# Revit family: QPTW
name_source: partatom
category: Mechanical Equipment
revit_build: Autodesk Revit 2018 (Build: 20170223_1515(x64)
units: mm (PartAtom-declared; Revit-internal decimal feet)

## family parameters
Always vertical = Yes
Cut with Voids When Loaded = No
Part Type = Normal
Room Calculation Point = No
Round Connector Dimension = Use Radius
Shared = No
Work Plane-Based = No

## types (104) — shared parameters
Description = Series Fan Powered Air Terminal with Hot Water Coil
Enclosure Depth = 6 1/2"
Filter = 1"
HWC B = 1 3/4"
HWC C = 1 5/8"
HWC Length = 4"
HWC V = 9/16"
Manufacturer = Anemostat
Model = QPTW
URL = http://www.anemostat.com

## per-type parameters (varying)
| type | Diameter | Duct Inlet Radius | HWC "X" | HWC "Y" | HWC Conn Dia | HWC R | HWC-Z | Height | Induction | Induction Height "D" | Induction Width "C" | Length | Q5 Sound Elbow | Q5B | Q5Q | Radius | Width |
| 25012 QPTW 1/2-hp - 12" 1RC with S/Elbow | 11 7/8" | 6" | 20" | 17 1/2" | 7/8" | 7/16" | 12 1/4" | 18" | No | 16" | 17" | 34" | Yes | 20" | 18" | 5 15/16" | 40" |
| 37512 QPTW 3/4-hp - 12" 1RC W/Out S/Elbow | 11 7/8" | 6" | 24" | 17 1/2" | 7/8" | 7/16" | 12 1/4" | 20" | Yes | 18" | 21" | 40" | No | 23" | 20" | 5 15/16" | 46" |
| 37512 QPTW 3/4-hp - 12" 2RC W/Out S/Elbow | 11 7/8" | 6" | 24" | 17 1/2" | 7/8" | 7/16" | 13 1/2" | 20" | Yes | 18" | 21" | 40" | No | 23" | 20" | 5 15/16" | 46" |
| 37512 QPTW 3/4-hp - 12" 1RC with S/Elbow | 11 7/8" | 6" | 24" | 17 1/2" | 7/8" | 7/16" | 12 1/4" | 20" | No | 18" | 21" | 40" | Yes | 23" | 20" | 5 15/16" | 46" |
| 37512 QPTW 3/4-hp - 12" 2RC with S/Elbow | 11 7/8" | 6" | 24" | 17 1/2" | 7/8" | 7/16" | 13 1/2" | 20" | No | 18" | 21" | 40" | Yes | 23" | 20" | 5 15/16" | 46" |
| 37514 QPTW 3/4-hp - 14" 1RC W/Out S/Elbow | 13 7/8" | 7" | 24" | 17 1/2" | 7/8" | 7/16" | 12 1/4" | 20" | Yes | 18" | 21" | 40" | No | 23" | 20" | 6 15/16" | 46" |
| 37514 QPTW 3/4-hp - 14" 1RC with S/Elbow | 13 7/8" | 7" | 24" | 17 1/2" | 7/8" | 7/16" | 12 1/4" | 20" | No | 18" | 21" | 40" | Yes | 23" | 20" | 6 15/16" | 46" |
| 37514 QPTW 3/4-hp - 14" 2RC W/Out S/Elbow | 13 7/8" | 7" | 24" | 17 1/2" | 7/8" | 7/16" | 13 1/2" | 20" | Yes | 18" | 21" | 40" | No | 23" | 20" | 6 15/16" | 46" |
| 37514 QPTW 3/4-hp - 14" 2RC with S/Elbow | 13 7/8" | 7" | 24" | 17 1/2" | 7/8" | 7/16" | 13 1/2" | 20" | No | 18" | 21" | 40" | Yes | 23" | 20" | 6 15/16" | 46" |
| 37516 QPTW 3/4-hp - 16" 1RC W/Out S/Elbow | 15 7/8" | 8" | 24" | 17 1/2" | 7/8" | 7/16" | 12 1/4" | 20" | Yes | 18" | 21" | 40" | No | 23" | 20" | 7 15/16" | 46" |
| 37516 QPTW 3/4-hp - 16" 1RC with S/Elbow | 15 7/8" | 8" | 24" | 17 1/2" | 7/8" | 7/16" | 12 1/4" | 20" | No | 18" | 21" | 40" | Yes | 23" | 20" | 7 15/16" | 46" |
| 37516 QPTW 3/4-hp - 16" 2RC W/Out S/Elbow | 15 7/8" | 8" | 24" | 17 1/2" | 7/8" | 7/16" | 13 1/2" | 20" | Yes | 18" | 21" | 40" | No | 23" | 20" | 7 15/16" | 46" |
| 37516 QPTW 3/4-hp - 16" 2RC with S/Elbow | 15 7/8" | 8" | 24" | 17 1/2" | 7/8" | 7/16" | 13 1/2" | 20" | No | 18" | 21" | 40" | Yes | 23" | 20" | 7 15/16" | 46" |
| 12509 QPTW 1/4-hp - 09" 1RC with S/Elbow | 8 7/8" | 4" | 16" | 15" | 1/2" | 1/4" | 12 1/4" | 15" | No | 12" | 13" | 30" | Yes | 18" | 18" | 4 7/16" | 34" |
| 12509 QPTW 1/4-hp - 09" 1RC W/Out S/Elbow | 8 7/8" | 4" | 16" | 15" | 1/2" | 1/4" | 12 1/4" | 15" | Yes | 12" | 13" | 30" | No | 18" | 18" | 4 7/16" | 34" |
| 25012 QPTW 1/2-hp - 12" 1RC W/Out S/Elbow | 11 7/8" | 6" | 20" | 17 1/2" | 7/8" | 7/16" | 12 1/4" | 18" | Yes | 16" | 17" | 34" | No | 20" | 18" | 5 15/16" | 40" |
| 35016 QPTW 1/2-hp - 16" 1RC with S/Elbow | 15 7/8" | 8" | 24" | 17 1/2" | 7/8" | 7/16" | 12 1/4" | 20" | No | 18" | 21" | 40" | Yes | 23" | 20" | 7 15/16" | 46" |
| 35016 QPTW 1/2-hp - 16" 2RC W/Out S/Elbow | 15 7/8" | 8" | 24" | 17 1/2" | 7/8" | 7/16" | 13 1/2" | 20" | Yes | 18" | 21" | 40" | No | 23" | 20" | 7 15/16" | 46" |
| 35016 QPTW 1/2-hp - 16" 1RC W/Out S/Elbow | 15 7/8" | 8" | 24" | 17 1/2" | 7/8" | 7/16" | 12 1/4" | 20" | Yes | 18" | 21" | 40" | No | 23" | 20" | 7 15/16" | 46" |
| 35016 QPTW 1/2-hp - 16" 2RC with S/Elbow | 15 7/8" | 8" | 24" | 17 1/2" | 7/8" | 7/16" | 13 1/2" | 20" | No | 18" | 21" | 40" | Yes | 23" | 20" | 7 15/16" | 46" |
| 35014 QPTW 1/2-hp - 14" 1RC W/Out S/Elbow | 13 7/8" | 7" | 24" | 17 1/2" | 7/8" | 7/16" | 12 1/4" | 20" | Yes | 18" | 21" | 40" | No | 23" | 20" | 6 15/16" | 46" |
| 35014 QPTW 1/2-hp - 14" 1RC with S/Elbow | 13 7/8" | 7" | 24" | 17 1/2" | 7/8" | 7/16" | 12 1/4" | 20" | No | 18" | 21" | 40" | Yes | 23" | 20" | 6 15/16" | 46" |
| 35014 QPTW 1/2-hp - 14" 2RC W/Out S/Elbow | 15 7/8" | 8" | 24" | 17 1/2" | 7/8" | 7/16" | 13 1/2" | 20" | Yes | 18" | 21" | 40" | No | 23" | 20" | 7 15/16" | 46" |
| 35014 QPTW 1/2-hp - 14" 2RC with S/Elbow | 15 7/8" | 8" | 24" | 17 1/2" | 7/8" | 7/16" | 13 1/2" | 20" | No | 18" | 21" | 40" | Yes | 23" | 20" | 7 15/16" | 46" |
| 35012 QPTW 1/2-hp - 12" 2RC with S/Elbow | 11 7/8" | 6" | 24" | 17 1/2" | 7/8" | 7/16" | 13 1/2" | 20" | No | 18" | 21" | 40" | Yes | 23" | 20" | 5 15/16" | 46" |
| 35012 QPTW 1/2-hp - 12" 2RC W/Out S/Elbow | 11 7/8" | 6" | 24" | 17 1/2" | 7/8" | 7/16" | 13 1/2" | 20" | Yes | 18" | 21" | 40" | No | 23" | 20" | 5 15/16" | 46" |
| 35012 QPTW 1/2-hp - 12" 1RC with S/Elbow | 11 7/8" | 6" | 24" | 17 1/2" | 7/8" | 7/16" | 12 1/4" | 20" | No | 18" | 21" | 40" | Yes | 23" | 20" | 5 15/16" | 46" |
| 35012 QPTW 1/2-hp - 12" 1RC W/Out S/Elbow | 11 7/8" | 6" | 24" | 17 1/2" | 7/8" | 7/16" | 12 1/4" | 20" | Yes | 18" | 21" | 40" | No | 23" | 20" | 5 15/16" | 46" |
| 31016 QPTW 1-hp - 16" 2RC with S/Elbow | 15 7/8" | 8" | 24" | 17 1/2" | 7/8" | 7/16" | 13 1/2" | 20" | No | 18" | 21" | 40" | Yes | 23" | 20" | 7 15/16" | 46" |
| 31016 QPTW 1-hp - 16" 2RC W/Out S/Elbow | 15 7/8" | 8" | 24" | 17 1/2" | 7/8" | 7/16" | 13 1/2" | 20" | Yes | 18" | 21" | 40" | No | 23" | 20" | 7 15/16" | 46" |
| 31016 QPTW 1-hp - 16" 1RC with S/Elbow | 15 7/8" | 8" | 24" | 17 1/2" | 7/8" | 7/16" | 12 1/4" | 20" | No | 18" | 21" | 40" | Yes | 23" | 20" | 7 15/16" | 46" |
| 31016 QPTW 1-hp - 16" 1RC W/Out S/Elbow | 15 7/8" | 8" | 24" | 17 1/2" | 7/8" | 7/16" | 12 1/4" | 20" | Yes | 18" | 21" | 40" | No | 23" | 20" | 7 15/16" | 46" |
| 31014 QPTW 1-hp - 14" 1RC W/Out S/Elbow | 13 7/8" | 7" | 24" | 17 1/2" | 7/8" | 7/16" | 12 1/4" | 20" | Yes | 18" | 21" | 40" | No | 23" | 20" | 6 15/16" | 46" |
| 31014 QPTW 1-hp - 14" 1RC with S/Elbow | 13 7/8" | 7" | 24" | 17 1/2" | 7/8" | 7/16" | 12 1/4" | 20" | No | 18" | 21" | 40" | Yes | 23" | 20" | 6 15/16" | 46" |
| 31014 QPTW 1-hp - 14" 2RC W/Out S/Elbow | 13 7/8" | 7" | 24" | 17 1/2" | 7/8" | 7/16" | 13 1/2" | 20" | Yes | 18" | 21" | 40" | No | 23" | 20" | 6 15/16" | 46" |
| 31014 QPTW 1-hp - 14" 2RC with S/Elbow | 13 7/8" | 7" | 24" | 17 1/2" | 7/8" | 7/16" | 13 1/2" | 20" | No | 18" | 21" | 40" | Yes | 23" | 20" | 6 15/16" | 46" |
| 31012 QPTW 1-hp - 12" 1RC W/Out S/Elbow | 11 7/8" | 6" | 24" | 17 1/2" | 7/8" | 7/16" | 12 1/4" | 20" | Yes | 18" | 21" | 40" | No | 23" | 20" | 5 15/16" | 46" |
| 31012 QPTW 1-hp - 12" 1RC with S/Elbow | 11 7/8" | 6" | 24" | 17 1/2" | 7/8" | 7/16" | 12 1/4" | 20" | No | 18" | 21" | 40" | Yes | 23" | 20" | 5 15/16" | 46" |
| 31012 QPTW 1-hp - 12" 2RC W/Out S/Elbow | 11 7/8" | 6" | 24" | 17 1/2" | 7/8" | 7/16" | 13 1/2" | 20" | Yes | 18" | 21" | 40" | No | 23" | 20" | 5 15/16" | 46" |
| 31012 QPTW 1-hp - 12" 2RC with S/Elbow | 11 7/8" | 6" | 24" | 17 1/2" | 7/8" | 7/16" | 13 1/2" | 20" | No | 18" | 21" | 40" | Yes | 23" | 20" | 5 15/16" | 46" |
| 25012 QPTW 1/2-hp - 12" 2RC W/Out S/Elbow | 11 7/8" | 6" | 20" | 17 1/2" | 7/8" | 7/16" | 13 1/2" | 18" | Yes | 16" | 17" | 34" | No | 20" | 18" | 5 15/16" | 40" |
| 25012 QPTW 1/2-hp - 12" 2RC with S/Elbow | 11 7/8" | 6" | 20" | 17 1/2" | 7/8" | 7/16" | 13 1/2" | 18" | No | 16" | 17" | 34" | Yes | 20" | 18" | 5 15/16" | 40" |
| 25010 QPTW 1/2-hp - 10" 2RC with S/Elbow | 9 7/8" | 5" | 20" | 17 1/2" | 7/8" | 7/16" | 13 1/2" | 18" | No | 16" | 17" | 34" | Yes | 20" | 18" | 4 15/16" | 40" |
| 25010 QPTW 1/2-hp - 10" 2RC W/Out S/Elbow | 9 7/8" | 5" | 20" | 17 1/2" | 7/8" | 7/16" | 13 1/2" | 18" | Yes | 16" | 17" | 34" | No | 20" | 18" | 4 15/16" | 40" |
| 25010 QPTW 1/2-hp - 10" 1RC with S/Elbow | 9 7/8" | 5" | 20" | 17 1/2" | 7/8" | 7/16" | 12 1/4" | 18" | No | 16" | 17" | 34" | Yes | 20" | 18" | 4 15/16" | 40" |
| 25010 QPTW 1/2-hp - 10" 1RC W/Out S/Elbow | 9 7/8" | 5" | 20" | 17 1/2" | 7/8" | 7/16" | 12 1/4" | 18" | Yes | 16" | 17" | 34" | No | 20" | 18" | 4 15/16" | 40" |
| 25009 QPTW 1/2-hp - 09" 1RC W/Out S/Elbow | 8 7/8" | 4" | 20" | 17 1/2" | 7/8" | 7/16" | 12 1/4" | 18" | Yes | 16" | 17" | 34" | No | 20" | 18" | 4 7/16" | 40" |
| 25009 QPTW 1/2-hp - 09" 1RC with S/Elbow | 8 7/8" | 4" | 20" | 17 1/2" | 7/8" | 7/16" | 12 1/4" | 18" | No | 16" | 17" | 34" | Yes | 20" | 18" | 4 7/16" | 40" |
| 25009 QPTW 1/2-hp - 09" 2RC W/Out S/Elbow | 8 7/8" | 4" | 20" | 17 1/2" | 7/8" | 7/16" | 13 1/2" | 18" | Yes | 16" | 17" | 34" | No | 20" | 18" | 4 7/16" | 40" |
| 25009 QPTW 1/2-hp - 09" 2RC with S/Elbow | 8 7/8" | 4" | 20" | 17 1/2" | 7/8" | 7/16" | 13 1/2" | 18" | No | 16" | 17" | 34" | Yes | 20" | 18" | 4 7/16" | 40" |
| 12509 QPTW 1/4-hp - 09" 2RC W/Out S/Elbow | 8 7/8" | 4" | 16" | 15" | 1/2" | 1/4" | 13 1/2" | 15" | Yes | 12" | 13" | 30" | No | 18" | 18" | 4 7/16" | 34" |
| 12509 QPTW 1/4-hp - 09" 2RC with S/Elbow | 8 7/8" | 4" | 16" | 15" | 1/2" | 1/4" | 13 1/2" | 15" | No | 12" | 13" | 30" | Yes | 18" | 18" | 4 7/16" | 34" |
| 22512 QPTW 1/4-hp - 12" 1RC W/Out S/Elbow | 11 7/8" | 6" | 20" | 17 1/2" | 7/8" | 7/16" | 12 1/4" | 18" | Yes | 16" | 17" | 34" | No | 20" | 18" | 5 15/16" | 40" |
| 22512 QPTW 1/4-hp - 12" 1RC with S/Elbow | 11 7/8" | 6" | 20" | 17 1/2" | 7/8" | 7/16" | 12 1/4" | 18" | No | 16" | 17" | 34" | Yes | 20" | 18" | 5 15/16" | 40" |
| 22512 QPTW 1/4-hp - 12" 2RC W/Out S/Elbow | 11 7/8" | 6" | 20" | 17 1/2" | 7/8" | 7/16" | 13 1/2" | 18" | No | 16" | 17" | 34" | Yes | 20" | 18" | 5 15/16" | 40" |
| 22512 QPTW 1/4-hp - 12" 2RC with S/Elbow | 11 7/8" | 6" | 20" | 17 1/2" | 7/8" | 7/16" | 13 1/2" | 18" | No | 16" | 17" | 34" | Yes | 20" | 18" | 5 15/16" | 40" |
| 22510 QPTW 1/4-hp - 10" 1RC W/Out S/Elbow | 9 7/8" | 5" | 20" | 17 1/2" | 7/8" | 7/16" | 12 1/4" | 18" | Yes | 16" | 17" | 34" | No | 20" | 18" | 4 15/16" | 40" |
| 22509 QPTW 1/4-hp - 09" 1RC W/Out S/Elbow | 8 7/8" | 4" | 20" | 17 1/2" | 7/8" | 7/16" | 12 1/4" | 18" | Yes | 16" | 17" | 34" | No | 20" | 18" | 4 7/16" | 40" |
| 22510 QPTW 1/4-hp - 10" 1RC with S/Elbow | 9 7/8" | 5" | 20" | 17 1/2" | 7/8" | 7/16" | 12 1/4" | 18" | No | 16" | 17" | 34" | Yes | 20" | 18" | 4 15/16" | 40" |
| 22509 QPTW 1/4-hp - 09" 1RC with S/Elbow | 8 7/8" | 4" | 20" | 17 1/2" | 7/8" | 7/16" | 12 1/4" | 18" | No | 16" | 17" | 34" | Yes | 20" | 18" | 4 7/16" | 40" |
| 22509 QPTW 1/4-hp - 09" 2RC W/Out S/Elbow | 8 7/8" | 4" | 20" | 17 1/2" | 7/8" | 7/16" | 13 1/2" | 18" | Yes | 16" | 17" | 34" | No | 20" | 18" | 4 7/16" | 40" |
| 22509 QPTW 1/4-hp - 09" 2RC with S/Elbow | 8 7/8" | 4" | 20" | 17 1/2" | 7/8" | 7/16" | 13 1/2" | 18" | No | 16" | 17" | 34" | Yes | 20" | 18" | 4 7/16" | 40" |
| 22510 QPTW 1/4-hp - 10" 2RC W/Out S/Elbow | 9 7/8" | 5" | 20" | 17 1/2" | 7/8" | 7/16" | 13 1/2" | 18" | Yes | 16" | 17" | 34" | No | 20" | 18" | 4 15/16" | 40" |
| 22510 QPTW 1/4-hp - 10" 2RC with S/Elbow | 9 7/8" | 5" | 20" | 17 1/2" | 7/8" | 7/16" | 13 1/2" | 18" | No | 16" | 17" | 34" | Yes | 20" | 18" | 4 15/16" | 40" |
| 21709 QPTW 1/6-hp - 09" 1RC W/Out S/Elbow | 8 7/8" | 4" | 20" | 17 1/2" | 7/8" | 7/16" | 12 1/4" | 18" | Yes | 16" | 17" | 34" | No | 20" | 18" | 4 7/16" | 40" |
| 21709 QPTW 1/6-hp - 09" 1RC with S/Elbow | 8 7/8" | 4" | 20" | 17 1/2" | 7/8" | 7/16" | 12 1/4" | 18" | No | 16" | 17" | 34" | Yes | 20" | 18" | 4 7/16" | 40" |
| 21710 QPTW 1/6-hp - 10" 1RC W/Out S/Elbow | 9 7/8" | 5" | 20" | 17 1/2" | 7/8" | 7/16" | 12 1/4" | 18" | Yes | 16" | 17" | 34" | No | 20" | 18" | 4 15/16" | 40" |
| 21710 QPTW 1/6-hp - 10" 1RC with S/Elbow | 9 7/8" | 5" | 20" | 17 1/2" | 7/8" | 7/16" | 12 1/4" | 18" | No | 16" | 17" | 34" | Yes | 20" | 18" | 4 15/16" | 40" |
| 21709 QPTW 1/6-hp - 09" 2RC W/Out S/Elbow | 8 7/8" | 4" | 20" | 17 1/2" | 7/8" | 7/16" | 13 1/2" | 18" | Yes | 16" | 17" | 34" | No | 20" | 18" | 4 7/16" | 40" |
| 21709 QPTW 1/6-hp - 09" 2RC with S/Elbow | 8 7/8" | 4" | 20" | 17 1/2" | 7/8" | 7/16" | 13 1/2" | 18" | No | 16" | 17" | 34" | Yes | 20" | 18" | 4 7/16" | 40" |
| 21710 QPTW 1/6-hp - 10" 2RC W/Out S/Elbow | 9 7/8" | 5" | 20" | 17 1/2" | 7/8" | 7/16" | 13 1/2" | 18" | Yes | 16" | 17" | 34" | No | 20" | 18" | 4 15/16" | 40" |
| 21710 QPTW 1/6-hp - 10" 2RC withS/Elbow | 9 7/8" | 5" | 20" | 17 1/2" | 7/8" | 7/16" | 13 1/2" | 18" | No | 16" | 17" | 34" | Yes | 20" | 18" | 4 15/16" | 40" |
| 21712 QPTW 1/6-hp - 12" 2RC W/Out S/Elbow | 11 7/8" | 6" | 20" | 17 1/2" | 7/8" | 7/16" | 13 1/2" | 18" | Yes | 16" | 17" | 34" | No | 20" | 18" | 5 15/16" | 40" |
| 21712 QPTW 1/6-hp - 12" 2RC with S/Elbow | 11 7/8" | 6" | 20" | 17 1/2" | 7/8" | 7/16" | 13 1/2" | 18" | No | 16" | 17" | 34" | Yes | 20" | 18" | 5 15/16" | 40" |
| 21712 QPTW 1/6-hp - 12" 1RC W/Out S/Elbow | 11 7/8" | 6" | 20" | 17 1/2" | 7/8" | 7/16" | 12 1/4" | 18" | Yes | 16" | 17" | 34" | No | 20" | 18" | 5 15/16" | 40" |
| 21712 QPTW 1/6-hp - 12" 1RC with S/Elbow | 11 7/8" | 6" | 20" | 17 1/2" | 7/8" | 7/16" | 12 1/4" | 18" | No | 16" | 17" | 34" | Yes | 20" | 18" | 5 15/16" | 40" |
| 12508 QPTW 1/4-hp - 08" 2RC with S/Elbow | 7 7/8" | 4" | 16" | 15" | 1/2" | 1/4" | 13 1/2" | 15" | No | 12" | 13" | 30" | Yes | 18" | 18" | 3 15/16" | 34" |
| 12507 QPTW 1/4-hp - 07" 2RC with S/Elbow | 6 7/8" | 3" | 16" | 15" | 1/2" | 1/4" | 13 1/2" | 15" | No | 12" | 13" | 30" | Yes | 18" | 18" | 3 7/16" | 34" |
| 12506 QPTW 1/4-hp - 06" 2RC with S/Elbow | 5 7/8" | 3" | 16" | 15" | 1/2" | 1/4" | 13 1/2" | 15" | No | 12" | 13" | 30" | Yes | 18" | 18" | 2 15/16" | 34" |
| 12508 QPTW 1/4-hp - 08" 1RC W/Out S/Elbow | 7 7/8" | 4" | 16" | 15" | 1/2" | 1/4" | 12 1/4" | 15" | Yes | 12" | 13" | 30" | No | 18" | 18" | 3 15/16" | 34" |
| 12507 QPTW 1/4-hp - 07" 1RC W/Out S/Elbow | 6 7/8" | 3" | 16" | 15" | 1/2" | 1/4" | 12 1/4" | 15" | Yes | 12" | 13" | 30" | No | 18" | 18" | 3 7/16" | 34" |
| 12506 QPTW 1/4-hp - 06" 1RC W/Out S/Elbow | 5 7/8" | 3" | 16" | 15" | 1/2" | 1/4" | 12 1/4" | 15" | Yes | 12" | 13" | 30" | No | 18" | 18" | 2 15/16" | 34" |
| 12506 QPTW 1/4-hp - 06" 1RC with S/Elbow | 5 7/8" | 3" | 16" | 15" | 1/2" | 1/4" | 12 1/4" | 15" | No | 12" | 13" | 30" | Yes | 18" | 18" | 2 15/16" | 34" |
| 12506 QPTW 1/4-hp - 06" 2RC W/Out S/Elbow | 5 7/8" | 3" | 16" | 15" | 1/2" | 1/4" | 13 1/2" | 15" | Yes | 12" | 13" | 30" | No | 18" | 18" | 2 15/16" | 34" |
| 12507 QPTW 1/4-hp - 07" 1RC with S/Elbow | 6 7/8" | 3" | 16" | 15" | 1/2" | 1/4" | 12 1/4" | 15" | No | 12" | 13" | 30" | Yes | 18" | 18" | 3 7/16" | 34" |
| 12507 QPTW 1/4-hp - 07" 2RC W/Out S/Elbow | 6 7/8" | 3" | 16" | 15" | 1/2" | 1/4" | 13 1/2" | 15" | Yes | 12" | 13" | 30" | No | 18" | 18" | 3 7/16" | 34" |
| 12508 QPTW 1/4-hp - 08" 1RC with S/Elbow | 7 7/8" | 4" | 16" | 15" | 1/2" | 1/4" | 12 1/4" | 15" | No | 12" | 13" | 30" | Yes | 18" | 18" | 3 15/16" | 34" |
| 12508 QPTW 1/4-hp - 08" 2RC W/Out S/Elbow | 7 7/8" | 4" | 16" | 15" | 1/2" | 1/4" | 13 1/2" | 15" | Yes | 12" | 13" | 30" | No | 18" | 18" | 3 15/16" | 34" |
| 11706 QPTW 1/6-hp - 06" 1RC W/Out S/Elbow | 5 7/8" | 3" | 16" | 15" | 1/2" | 1/4" | 12 1/4" | 15" | Yes | 12" | 13" | 30" | No | 18" | 18" | 2 15/16" | 34" |
| 11706 QPTW 1/6-hp - 06" 1RC with S/Elbow | 5 7/8" | 3" | 16" | 15" | 1/2" | 1/4" | 12 1/4" | 15" | No | 12" | 13" | 30" | Yes | 18" | 18" | 2 15/16" | 34" |
| 11707 QPTW 1/6-hp - 07" 1RC W/Out S/Elbow | 6 7/8" | 3" | 16" | 15" | 1/2" | 1/4" | 12 1/4" | 15" | Yes | 12" | 13" | 30" | No | 18" | 18" | 3 7/16" | 34" |
| 11707 QPTW 1/6-hp - 07" 1RC with S/Elbow | 6 7/8" | 3" | 16" | 15" | 1/2" | 1/4" | 12 1/4" | 15" | No | 12" | 13" | 30" | Yes | 18" | 18" | 3 7/16" | 34" |
| 11708 QPTW 1/6-hp - 08" 1RC W/Out S/Elbow | 7 7/8" | 4" | 16" | 15" | 1/2" | 1/4" | 12 1/4" | 15" | Yes | 12" | 13" | 30" | No | 18" | 18" | 3 15/16" | 34" |
| 11708 QPTW 1/6-hp - 08" 1RC with S/Elbow | 7 7/8" | 4" | 16" | 15" | 1/2" | 1/4" | 12 1/4" | 15" | No | 12" | 13" | 30" | Yes | 18" | 18" | 3 15/16" | 34" |
| 11709 QPTW 1/6-hp - 09" 1RC W/Out S/Elbow | 8 7/8" | 4" | 16" | 15" | 1/2" | 1/4" | 12 1/4" | 15" | Yes | 12" | 13" | 30" | No | 18" | 18" | 4 7/16" | 34" |
| 11709 QPTW 1/6-hp - 09" 1RC with S/Elbow | 8 7/8" | 4" | 16" | 15" | 1/2" | 1/4" | 12 1/4" | 15" | No | 12" | 13" | 30" | Yes | 18" | 18" | 4 7/16" | 34" |
| 11706 QPTW 1/6-hp - 06" 2RC W/Out S/Elbow | 5 7/8" | 3" | 16" | 15" | 1/2" | 1/4" | 13 1/2" | 15" | Yes | 12" | 13" | 30" | No | 18" | 18" | 2 15/16" | 34" |
| 11706 QPTW 1/6-hp - 06" 2RC with S/Elbow | 5 7/8" | 3" | 16" | 15" | 1/2" | 1/4" | 13 1/2" | 15" | No | 12" | 13" | 30" | Yes | 18" | 18" | 2 15/16" | 34" |
| 11707 QPTW 1/6-hp - 07" 2RC W/Out S/Elbow | 6 7/8" | 3" | 16" | 15" | 1/2" | 1/4" | 13 1/2" | 15" | Yes | 12" | 13" | 30" | No | 18" | 18" | 3 7/16" | 34" |
| 11707 QPTW 1/6-hp - 07" 2RC with S/Elbow | 6 7/8" | 3" | 16" | 15" | 1/2" | 1/4" | 13 1/2" | 15" | No | 12" | 13" | 30" | Yes | 18" | 18" | 3 7/16" | 34" |
| 11708 QPTW 1/6-hp - 08" 2RC W/Out S/Elbow | 7 7/8" | 4" | 16" | 15" | 1/2" | 1/4" | 13 1/2" | 15" | Yes | 12" | 13" | 30" | No | 18" | 18" | 3 15/16" | 34" |
| 11708 QPTW 1/6-hp - 08" 2RC with S/Elbow | 7 7/8" | 4" | 16" | 15" | 1/2" | 1/4" | 13 1/2" | 15" | No | 12" | 13" | 30" | Yes | 18" | 18" | 3 15/16" | 34" |
| 11709 QPTW 1/6-hp - 09" 2RC W/Out S/Elbow | 8 7/8" | 4" | 16" | 15" | 1/2" | 1/4" | 13 1/2" | 15" | Yes | 12" | 13" | 30" | No | 18" | 18" | 4 7/16" | 34" |
| 11709 QPTW 1/6-hp - 09" 2RC with S/Elbow | 8 7/8" | 4" | 16" | 15" | 1/2" | 1/4" | 13 1/2" | 15" | No | 12" | 13" | 30" | Yes | 18" | 18" | 4 7/16" | 34" |

## geometry (parser evidence)
native form markers: Sweep x3
no freeform markers — native parametric forms only
